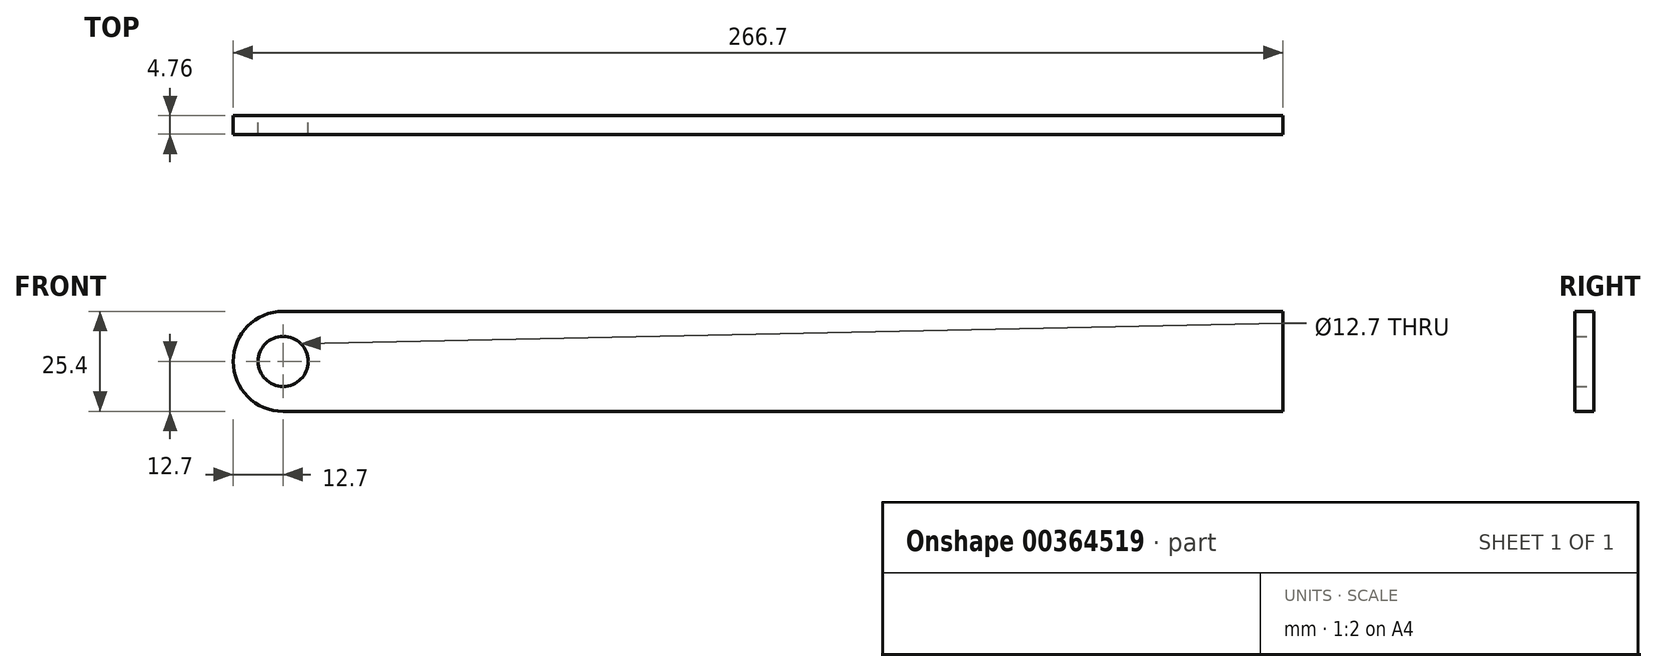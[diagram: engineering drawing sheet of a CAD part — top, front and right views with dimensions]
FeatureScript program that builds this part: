
annotation { "Feature Type Name" : "Feature", "Feature Type Description" : "" }
export const myFeature = defineFeature(function(context is Context, id is Id, definition is map)
    precondition{}
    {
        {
            var Q0;
            Q0=qCreatedBy(makeId("Front.planeOp"),FACE);
            var sketch = newSketch(context, id + "F0", { "sketchPlane" : qUnion([Q0])});
            skLineSegment(sketch, "E0", {"start": v(-127, 0) * mm, "end": v(127, 0) * mm, "construction": true});
            skArc(sketch, "E1.0.startCap", {"start": v(-127, -12.7) * mm, "mid": v(-139.7, 0) * mm, "end": v(-127, 12.7) * mm});
            skArc(sketch, "E1.0.endCap", {"start": v(127, 12.7) * mm, "mid": v(139.7, 0) * mm, "end": v(127, -12.7) * mm, "construction": true});
            skLineSegment(sketch, "E1.0.left", {"start": v(-127, 12.7) * mm, "end": v(127, 12.7) * mm});
            skLineSegment(sketch, "E1.0.right", {"start": v(-127, -12.7) * mm, "end": v(127, -12.7) * mm});
            skCircle(sketch, "E2", {"center": v(-127, 0) * mm, "radius": 6.35 * mm});
            skLineSegment(sketch, "E3", {"start": v(127, 12.7) * mm, "end": v(127, -12.7) * mm});
            skSolve(sketch);
        }
        {
            var Q0;
            Q0 = qSketchRegion(id + "F0", true);
            extrude(context, id + "F1", {"entities" : qUnion([Q0]), "endBound" : BoundingType.SYMMETRIC, "depth" : 4.76 * mm});
        }
    });
